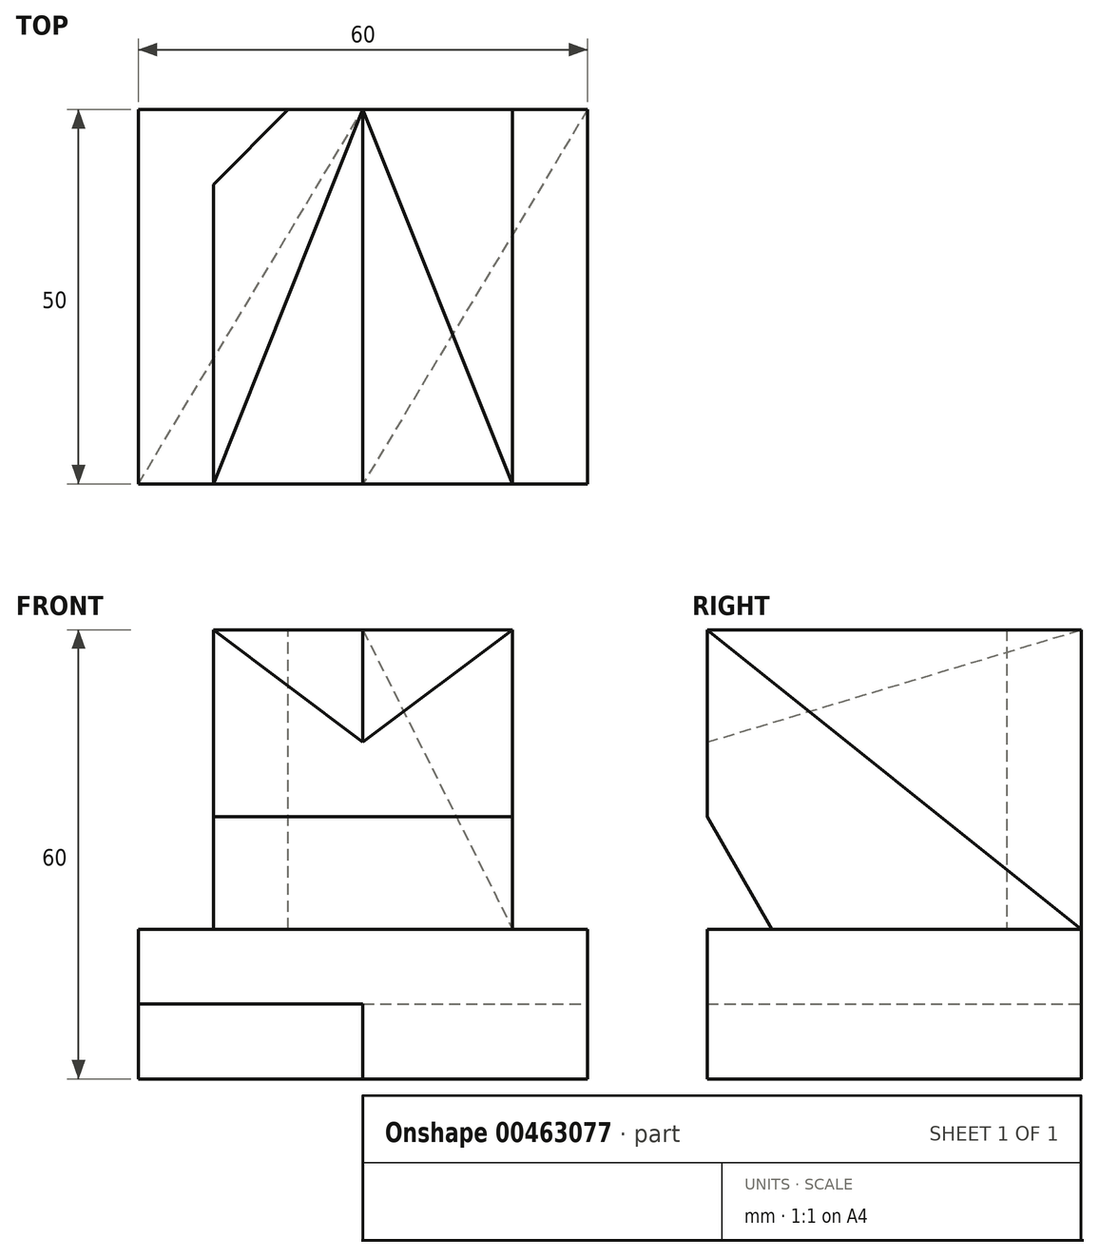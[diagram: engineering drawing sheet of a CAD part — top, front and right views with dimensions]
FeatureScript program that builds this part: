
annotation { "Feature Type Name" : "Feature", "Feature Type Description" : "" }
export const myFeature = defineFeature(function(context is Context, id is Id, definition is map)
    precondition{}
    {
        {
            var Q0;
            Q0=qCreatedBy(makeId("Top.planeOp"),FACE);
            var sketch = newSketch(context, id + "F0", { "sketchPlane" : qUnion([Q0])});
            skLineSegment(sketch, "E0.bottom", {"start": v(-30, 22.76) * mm, "end": v(30, 22.76) * mm});
            skLineSegment(sketch, "E0.top", {"start": v(-30, -27.24) * mm, "end": v(30, -27.24) * mm});
            skLineSegment(sketch, "E0.left", {"start": v(-30, 22.76) * mm, "end": v(-30, -27.24) * mm});
            skLineSegment(sketch, "E0.right", {"start": v(30, 22.76) * mm, "end": v(30, -27.24) * mm});
            skSolve(sketch);
        }
        {
            var Q0;
            Q0 = qSketchRegion(id + "F0", true);
            extrude(context, id + "F1", {"entities" : qUnion([Q0]), "depth" : 20 * mm});
        }
        {
            var Q0;
            Q0=makeQuery(id+"F1.opExtrude","CAP_FACE",FACE,{"disambiguationData":[OSD([sQuery(id+"F0.wireOp",EDGE,"E0.bottom"),sQuery(id+"F0.wireOp",EDGE,"E0.top"),sQuery(id+"F0.wireOp",EDGE,"E0.left"),sQuery(id+"F0.wireOp",EDGE,"E0.right")])],"isStart":false});
            var sketch = newSketch(context, id + "F2", { "sketchPlane" : qUnion([Q0])});
            skLineSegment(sketch, "E1.bottom", {"start": v(-20, 22.76) * mm, "end": v(20, 22.76) * mm});
            skLineSegment(sketch, "E1.top", {"start": v(-20, -27.24) * mm, "end": v(20, -27.24) * mm});
            skLineSegment(sketch, "E1.left", {"start": v(-20, 22.76) * mm, "end": v(-20, -27.24) * mm});
            skLineSegment(sketch, "E1.right", {"start": v(20, 22.76) * mm, "end": v(20, -27.24) * mm});
            skSolve(sketch);
        }
        {
            var Q0;
            Q0 = qSketchRegion(id + "F2", true);
            extrude(context, id + "F3", {"entities" : qUnion([Q0]), "operationType" : NewBodyOperationType.ADD, "depth" : 40 * mm});
        }
        {
            var Q0;
            Q0=makeQuery(id+"F3.opExtrude","SWEPT_FACE",FACE,{"disambiguationData":[OSD([sQuery(id+"F2.wireOp",EDGE,"E1.right")])]});
            var sketch = newSketch(context, id + "F4", { "sketchPlane" : qUnion([Q0])});
            skLineSegment(sketch, "E2", {"start": v(-27.24, 35) * mm, "end": v(-18.58, 20) * mm});
            skLineSegment(sketch, "E3", {"start": v(-18.58, 20) * mm, "end": v(-27.24, 20) * mm});
            skLineSegment(sketch, "E4", {"start": v(-27.24, 20) * mm, "end": v(-27.24, 35) * mm});
            skSolve(sketch);
        }
        {
            var Q0;
            Q0 = qSketchRegion(id + "F4", true);
            extrude(context, id + "F5", {"entities" : qUnion([Q0]), "operationType" : NewBodyOperationType.REMOVE, "endBound" : BoundingType.UP_TO_NEXT, "oppositeDirection" : true, "depth" : 25 * mm});
        }
        {
            var Q0;
            Q0=makeQuery(id+"F1.opExtrude","CAP_FACE",FACE,{"disambiguationData":[OSD([sQuery(id+"F0.wireOp",EDGE,"E0.bottom"),sQuery(id+"F0.wireOp",EDGE,"E0.top"),sQuery(id+"F0.wireOp",EDGE,"E0.left"),sQuery(id+"F0.wireOp",EDGE,"E0.right")])],"isStart":true});
            var sketch = newSketch(context, id + "F6", { "sketchPlane" : qUnion([Q0])});
            skLineSegment(sketch, "E5", {"start": v(-30, 27.24) * mm, "end": v(0, -22.76) * mm});
            skLineSegment(sketch, "E6", {"start": v(0, -22.76) * mm, "end": v(30, -22.76) * mm});
            skLineSegment(sketch, "E7", {"start": v(30, -22.76) * mm, "end": v(0, 27.24) * mm});
            skLineSegment(sketch, "E8", {"start": v(0, 27.24) * mm, "end": v(-30, 27.24) * mm});
            skSolve(sketch);
        }
        {
            var Q0;
            Q0 = qSketchRegion(id + "F6", true);
            extrude(context, id + "F7", {"entities" : qUnion([Q0]), "operationType" : NewBodyOperationType.REMOVE, "oppositeDirection" : true, "depth" : 10 * mm});
        }
        {
            var Q0;
            {var subQ1=sQuery(id+"F2.wireOp",EDGE,"E1.left");var subQ2=sQuery(id+"F2.wireOp",EDGE,"E1.top");Q0=makeQuery(id+"F5.boolean.opBoolean","SPLIT",FACE,{"disambiguationData":[TD([makeQuery(id+"F3.opExtrude","SWEPT_FACE",FACE,{"disambiguationData":[OSD([subQ1])]})])],"derivedFrom":makeQuery(id+"F3.boolean.opBoolean","MERGE",FACE,{"derivedFrom":[makeQuery(id+"F1.opExtrude","SWEPT_FACE",FACE,{"disambiguationData":[OSD([sQuery(id+"F0.wireOp",EDGE,"E0.top")])]}),makeQuery(id+"F3.opExtrude","SWEPT_FACE",FACE,{"disambiguationData":[OSD([subQ2])]})]})});}
            var sketch = newSketch(context, id + "F8", { "sketchPlane" : qUnion([Q0])});
            skLineSegment(sketch, "E9", {"start": v(-20, 60) * mm, "end": v(0, 45) * mm});
            skLineSegment(sketch, "E10", {"start": v(0, 45) * mm, "end": v(20, 60) * mm});
            skLineSegment(sketch, "E11", {"start": v(20, 60) * mm, "end": v(-20, 60) * mm});
            skSolve(sketch);
        }
        {
            var Q0;
            Q0=makeQuery(id+"F3.opExtrude","SWEPT_FACE",FACE,{"disambiguationData":[OSD([sQuery(id+"F2.wireOp",EDGE,"E1.right")])]});
            var sketch = newSketch(context, id + "F9", { "sketchPlane" : qUnion([Q0])});
            skLineSegment(sketch, "E12", {"start": v(-27.24, 60) * mm, "end": v(-27.24, 45) * mm});
            skLineSegment(sketch, "E13", {"start": v(-27.24, 45) * mm, "end": v(22.76, 60) * mm});
            skLineSegment(sketch, "E14", {"start": v(22.76, 60) * mm, "end": v(-27.24, 60) * mm});
            skSolve(sketch);
        }
        {
            var Q0;
            Q0=makeQuery(id+"F8.imprint","IMPRINT",FACE,{"disambiguationData":[TD([[makeQuery(id+"F8.imprint","IMPRINT",EDGE,{"derivedFrom":sQuery(id+"F8.wireOp",EDGE,"E9")}),1.0]])]});
            var Q1;
            Q1=sQuery(id+"F9.wireOp",EDGE,"E13");
            sweep(context, id + "F10", {"operationType" : NewBodyOperationType.REMOVE, "profiles" : qUnion([Q0]), "path" : qUnion([Q1])});
        }
        {
            var Q0;
            Q0=makeQuery(id+"F3.boolean.opBoolean","MERGE",FACE,{"derivedFrom":[makeQuery(id+"F1.opExtrude","SWEPT_FACE",FACE,{"disambiguationData":[OSD([sQuery(id+"F0.wireOp",EDGE,"E0.bottom")])]}),makeQuery(id+"F3.opExtrude","SWEPT_FACE",FACE,{"disambiguationData":[OSD([sQuery(id+"F2.wireOp",EDGE,"E1.bottom")])]})]});
            var sketch = newSketch(context, id + "F11", { "sketchPlane" : qUnion([Q0])});
            skLineSegment(sketch, "E15", {"start": v(-20, 60) * mm, "end": v(0, 60) * mm});
            skLineSegment(sketch, "E16", {"start": v(0, 60) * mm, "end": v(-20, 20) * mm});
            skLineSegment(sketch, "E17", {"start": v(-20, 20) * mm, "end": v(-20, 60) * mm});
            skSolve(sketch);
        }
        {
            var Q0;
            Q0=makeQuery(id+"F3.opExtrude","SWEPT_FACE",FACE,{"disambiguationData":[OSD([sQuery(id+"F2.wireOp",EDGE,"E1.right")])]});
            var sketch = newSketch(context, id + "F12", { "sketchPlane" : qUnion([Q0])});
            skLineSegment(sketch, "E18", {"start": v(-27.24, 60) * mm, "end": v(22.76, 20) * mm});
            skLineSegment(sketch, "E19", {"start": v(22.76, 20) * mm, "end": v(22.76, 60) * mm});
            skLineSegment(sketch, "E20", {"start": v(22.76, 60) * mm, "end": v(-27.24, 60) * mm});
            skSolve(sketch);
        }
        {
            var Q0;
            Q0=makeQuery(id+"F11.imprint","IMPRINT",FACE,{"disambiguationData":[TD([[makeQuery(id+"F11.imprint","IMPRINT",EDGE,{"derivedFrom":sQuery(id+"F11.wireOp",EDGE,"E15")}),1.0]])]});
            var Q1;
            Q1=sQuery(id+"F12.wireOp",EDGE,"E18");
            sweep(context, id + "F13", {"operationType" : NewBodyOperationType.REMOVE, "profiles" : qUnion([Q0]), "path" : qUnion([Q1])});
        }
        {
            var Q0;
            Q0=makeQuery(id+"F3.opExtrude","SWEPT_EDGE",EDGE,{"disambiguationData":[OSD([sQuery(id+"F0.wireOp",EDGE,"E0.bottom"),sQuery(id+"F2.wireOp",EDGE,"E1.bottom"),sQuery(id+"F2.wireOp",EDGE,"E1.left")])]});
            chamfer(context, id + "F14", {"entities" : qUnion([Q0]), "width" : 10 * mm, "tangentPropagation" : true});
        }
    });
